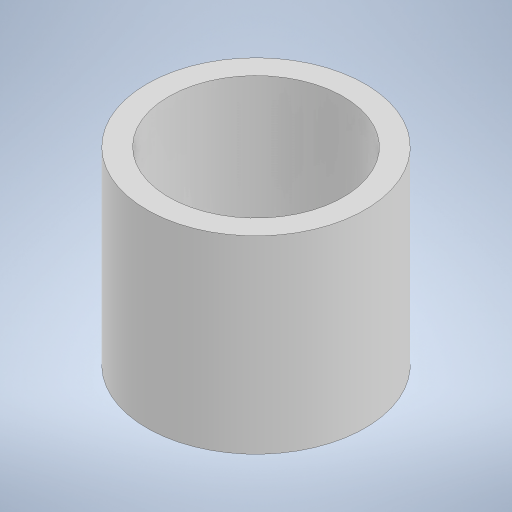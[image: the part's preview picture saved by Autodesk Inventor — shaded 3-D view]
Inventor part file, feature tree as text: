
AUTODESK INVENTOR PART (.ipt)
format: ipt  version: 2023 (Build 270158000, 158)  size: 237,568 bytes
history: native  units: mm
features: extrude x1, sketch x1
ambient origin geometry x8: Origin, YZ Plane, XZ Plane, XY Plane, X Axis, Y Axis, Z Axis, Center Point
bodies: Solid1 (feature_tree)
feature tree (2):
  extrude  "Extrusion1"  Depth=13.0mm
  sketch  "Sketch1"  dims[d0=12.0mm d1=15.0mm d2=13.0mm d3=0.0mm]
